# Revit family: Haworth_BuzziSpark_Sofa_TwoSeats_Open_AP_PRELIMINARY
name_source: partatom
category: Furniture
revit_build: Autodesk Revit 2018 (Build: 20170223_1515(x64)
units: mm (PartAtom-declared; Revit-internal decimal feet)

## family parameters
Always vertical = Yes
Cut with Voids When Loaded = No
OmniClass Number = 23.40.70.14.64.21
OmniClass Title = Systems Furniture
Room Calculation Point = No
Shared = No
Work Plane-Based = No

## types (5) — shared parameters
Actual Depth = 953 mm
Actual Width = 2391 mm
Arm Offset = 140 mm
Assembly Code = E2020200
Back Cushion Offset = 503 mm
Back Cushion Width = 981 mm
Back Upholstery Width = 1109 mm
Description = Haworth - BuzziSpark - Sofa - Two Seats - Open
Left tablet = Yes
Manufacturer = Haworth
Middle Leg Control = No
Model = Original AG 102
Revision Number = 1
Right Tablet = Yes
Seat Depth = 700 mm
Seat Height = 450 mm
Seat Offset = 555 mm
Seat Width = 1109 mm
Shield 1 Height = Haworth_BuzziSpark_Sofa_ShieldUpholstery_Part : Medium
Shield 2 Height = Haworth_BuzziSpark_Sofa_ShieldUpholstery_Part : Medium
Shield Width = 1150 mm
Shield w Tube Thickness = 86 mm
Side Upholstery Width = 648 mm
Size = Verify Final Dim. w/ Haworth
URL = https://www.haworth.com
URL - Product = https://www.haworth.com
Warranty = http://www.haworth.com
With Arm Cushion = Yes

## per-type parameters (varying)
| type | Left High Back | Left Low Back | Left Medium Back | Right High Back | Right Low Back | Right Medium Back |
| High - High | Yes | No | No | Yes | No | No |
| Low - Low | No | Yes | No | No | Yes | No |
| High - Medium | Yes | No | No | No | No | Yes |
| Medium - High | No | No | Yes | Yes | No | No |
| Medium - Medium | No | No | Yes | No | No | Yes |

## geometry (parser evidence)
native form markers: Extrusion x2, Sweep x24
no freeform markers — native parametric forms only
